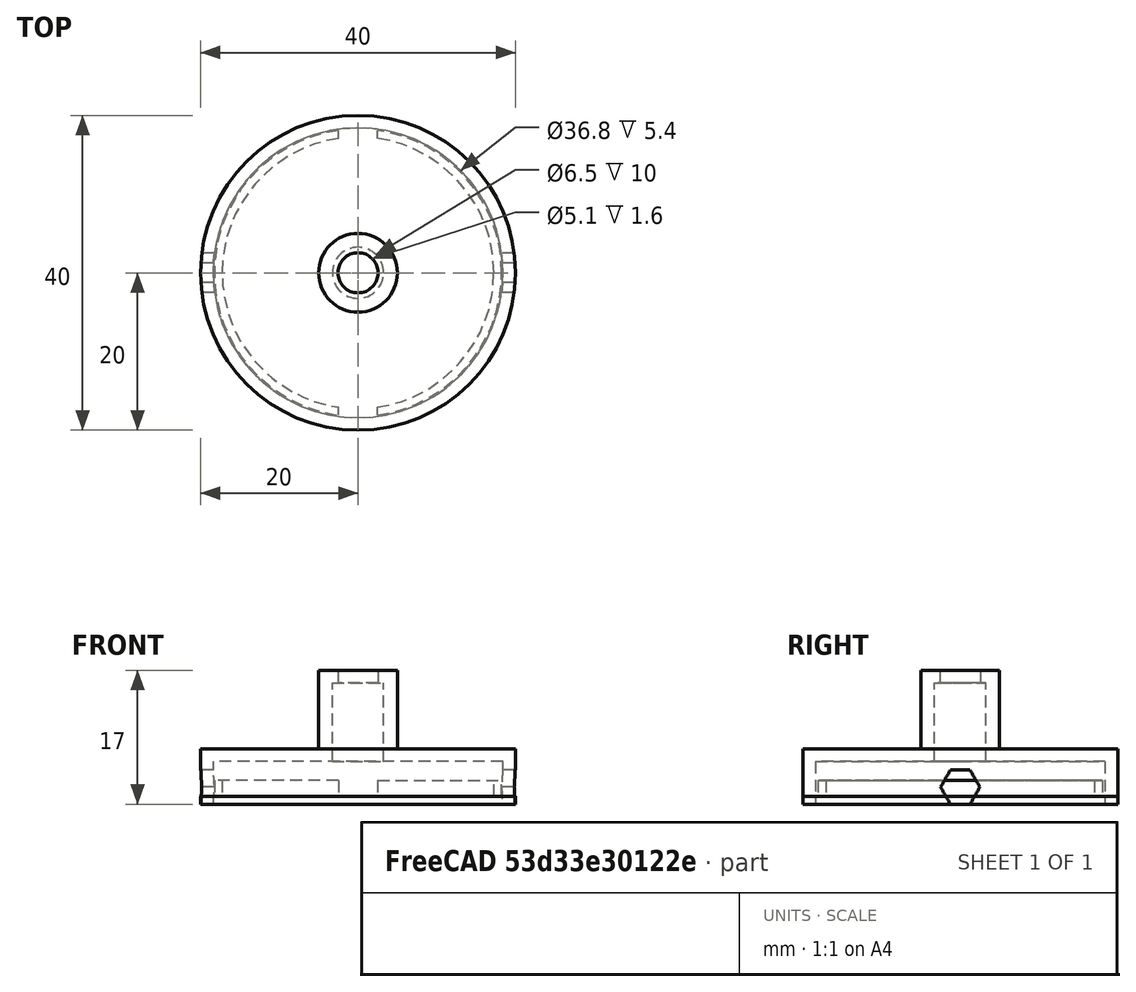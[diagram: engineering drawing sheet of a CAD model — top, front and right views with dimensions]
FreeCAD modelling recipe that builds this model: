
FCSTD DOCUMENT  (FreeCAD 0.19R18811 (Git))
Label: LEDLight
License: All rights reserved
LicenseURL: http://en.wikipedia.org/wiki/All_rights_reserved
objects: Sketcher::SketchObject×6, PartDesign::Pad×4, PartDesign::Thickness×2, PartDesign::Hole×2, PartDesign::Pocket×2, PartDesign::Body×2, Mesh::Feature×2
note: 26 computed .brp shape members not serialized (recipe doc carries the construction recipe); baked Part::Feature solids carry a one-line shape summary decoded from their .brp

FEATURE [Sketcher::SketchObject] Sketch
  MapMode = 5
  Support = -> [XY_Plane001]
  sketch-geometry (1):
    g0: Circle CenterX=0 CenterY=0 CenterZ=0 NormalX=0 NormalY=0 NormalZ=1 AngleXU=0 Radius=20
  constraints (2):
    c: Coincident(g0,g-1)
    c: Radius(g0) = 20
FEATURE [PartDesign::Pad] Pad
  Length = 7
  Length2 = 100
  Profile = -> Sketch
  Type = 0
FEATURE [Sketcher::SketchObject] Sketch001
  MapMode = 5
  Placement = pos=(0,0,7) rot=(0,0,1;0rad)
  Support = -> [Pad]
  sketch-geometry (1):
    g0: Circle CenterX=0 CenterY=0 CenterZ=0 NormalX=0 NormalY=0 NormalZ=1 AngleXU=0 Radius=5
  constraints (2):
    c: Coincident(g0,g-1)
    c: Radius(g0) = 5
FEATURE [PartDesign::Thickness] Thickness
  Base = -> Pad [Face2]
  BaseFeature = -> Pad
  Intersection = false
  Join = 0
  Mode = 0
  Reversed = true
  Value = 1.6
FEATURE [PartDesign::Pad] Pad001
  BaseFeature = -> Thickness
  Length = 10
  Length2 = 100
  Profile = -> Sketch001
  Type = 0
FEATURE [PartDesign::Hole] Hole
  BaseFeature = -> Pad001
  Depth = 2.5
  DepthType = 0
  Diameter = 5.1
  DrillPoint = 0
  DrillPointAngle = 118
  HoleCutCountersinkAngle = 90
  HoleCutDepth = 0
  HoleCutDiameter = 0
  HoleCutType = 0
  ModelActualThread = false
  Profile = -> Pad001 [Face7]
  Tapered = false
  TaperedAngle = 90
  ThreadAngle = 0
  ThreadClass = 0
  ThreadCutOffInner = 0
  ThreadCutOffOuter = 0
  ThreadDirection = 0
  ThreadFit = 0
  ThreadPitch = 0
  ThreadSize = 0
  ThreadType = 0
  Threaded = false
FEATURE [PartDesign::Hole] Hole001
  BaseFeature = -> Hole
  Depth = 10
  DepthType = 0
  Diameter = 6.5
  DrillPoint = 0
  DrillPointAngle = 118
  HoleCutCountersinkAngle = 90
  HoleCutDepth = 0
  HoleCutDiameter = 0
  HoleCutType = 0
  ModelActualThread = false
  Profile = -> Hole [Face6]
  Tapered = false
  TaperedAngle = 90
  ThreadAngle = 0
  ThreadClass = 0
  ThreadCutOffInner = 0
  ThreadCutOffOuter = 0
  ThreadDirection = 0
  ThreadFit = 0
  ThreadPitch = 0
  ThreadSize = 0
  ThreadType = 0
  Threaded = false
FEATURE [Sketcher::SketchObject] Sketch002
  MapMode = 5
  Placement = pos=(0,0,0) rot=(0.57735,0.57735,0.57735;2.0944rad)
  Support = -> [YZ_Plane001]
  sketch-geometry (7):
    g0: LineSegment StartX=1.25 StartY=0 StartZ=0 EndX=2.5 EndY=2.16506 EndZ=0
    g1: LineSegment StartX=2.5 StartY=2.16506 StartZ=0 EndX=1.25 EndY=4.33013 EndZ=0
    g2: LineSegment StartX=1.25 StartY=4.33013 StartZ=0 EndX=-1.25 EndY=4.33013 EndZ=0
    g3: LineSegment StartX=-1.25 StartY=4.33013 StartZ=0 EndX=-2.5 EndY=2.16506 EndZ=0
    g4: LineSegment StartX=-2.5 StartY=2.16506 StartZ=0 EndX=-1.25 EndY=-6.62e-14 EndZ=0
    g5: LineSegment StartX=-1.25 StartY=-6.63e-14 StartZ=0 EndX=1.25 EndY=0 EndZ=0
    g6: Circle [constr] CenterX=0 CenterY=2.16506 CenterZ=0 NormalX=0 NormalY=0 NormalZ=1 AngleXU=0 Radius=2.5
  constraints (17):
    c: Coincident(g0,g1)
    c: Coincident(g1,g2)
    c: Coincident(g2,g3)
    c: Coincident(g3,g4)
    c: Coincident(g4,g5)
    c: Coincident(g5,g0)
    c: Equal(g0, g1-g5) x5
    c: PointOnObject(g0,g6)
    c: PointOnObject(g1,g6)
    c: PointOnObject(g2,g6)
    c: PointOnObject(g3,g6)
    c: PointOnObject(g4,g6)
    c: PointOnObject(g5,g6)
    c: PointOnObject(g5,g-1)
    c: Horizontal(g2)
    c: Radius(g6) = 2.5
    c: PointOnObject(g6,g-2)
FEATURE [PartDesign::Pocket] Pocket
  BaseFeature = -> Hole001
  Length = 40
  Length2 = 100
  Midplane = true
  Profile = -> Sketch002
  Type = 1
FEATURE [PartDesign::Body] Body001
  Group = -> [Sketch,Pad,Sketch001,Thickness,Pad001,Hole,Hole001,Sketch002,Pocket]
  Origin = -> Origin001
  Tip = -> Pocket
FEATURE [Mesh::Feature] Mesh  label="Pocket (Meshed)"
FEATURE [Sketcher::SketchObject] Sketch003
  MapMode = 5
  Support = -> [XY_Plane]
  sketch-geometry (1):
    g0: Circle CenterX=0 CenterY=0 CenterZ=0 NormalX=0 NormalY=0 NormalZ=1 AngleXU=0 Radius=20
  constraints (2):
    c: Coincident(g0,g-1)
    c: Radius(g0) = 20
FEATURE [PartDesign::Pad] Pad002
  Length = 1
  Length2 = 100
  Profile = -> Sketch003
  Type = 0
FEATURE [Sketcher::SketchObject] Sketch004
  MapMode = 5
  Placement = pos=(0,0,1) rot=(0,0,1;0rad)
  Support = -> [Pad002]
  sketch-geometry (1):
    g0: Circle CenterX=0 CenterY=0 CenterZ=0 NormalX=0 NormalY=0 NormalZ=1 AngleXU=0 Radius=18.25
  constraints (2):
    c: Coincident(g0,g-1)
    c: Diameter(g0) = 36.5
FEATURE [PartDesign::Pad] Pad003
  BaseFeature = -> Pad002
  Length = 2
  Length2 = 100
  Profile = -> Sketch004
  Type = 0
FEATURE [PartDesign::Thickness] Thickness001
  Base = -> Pad003 [Face5]
  BaseFeature = -> Pad003
  Intersection = true
  Join = 1
  Mode = 1
  Reversed = true
  Value = 1
FEATURE [Sketcher::SketchObject] Sketch005
  MapMode = 5
  Placement = pos=(0,0,0) rot=(1,0,0;1.5708rad)
  Support = -> [XZ_Plane]
  sketch-geometry (4):
    g0: LineSegment StartX=-2.5 StartY=3 StartZ=0 EndX=2.5 EndY=3 EndZ=0
    g1: LineSegment StartX=2.5 StartY=3 StartZ=0 EndX=2.5 EndY=1 EndZ=0
    g2: LineSegment StartX=2.5 StartY=1 StartZ=0 EndX=-2.5 EndY=1 EndZ=0
    g3: LineSegment StartX=-2.5 StartY=1 StartZ=0 EndX=-2.5 EndY=3 EndZ=0
  constraints (11):
    c: Coincident(g0,g1)
    c: Coincident(g1,g2)
    c: Coincident(g2,g3)
    c: Coincident(g3,g0)
    c: Horizontal(g0)
    c: Vertical(g1)
    c: Vertical(g3)
    c: DistanceY(g-1,g1) = 1
    c: DistanceY(g3,g3) = 2
    c: DistanceX(g0,g0) = 5
    c: Symmetric(g2,g1,g-2)
FEATURE [PartDesign::Pocket] Pocket001  label="Base001"
  BaseFeature = -> Thickness001
  Length = 5
  Length2 = 100
  Midplane = true
  Profile = -> Sketch005
  Type = 1
FEATURE [PartDesign::Body] Body  label="Base"
  Group = -> [Sketch003,Pad002,Sketch004,Pad003,Thickness001,Sketch005,Pocket001]
  Origin = -> Origin
  Tip = -> Pocket001
FEATURE [Mesh::Feature] Mesh001  label="Base Mesh"
